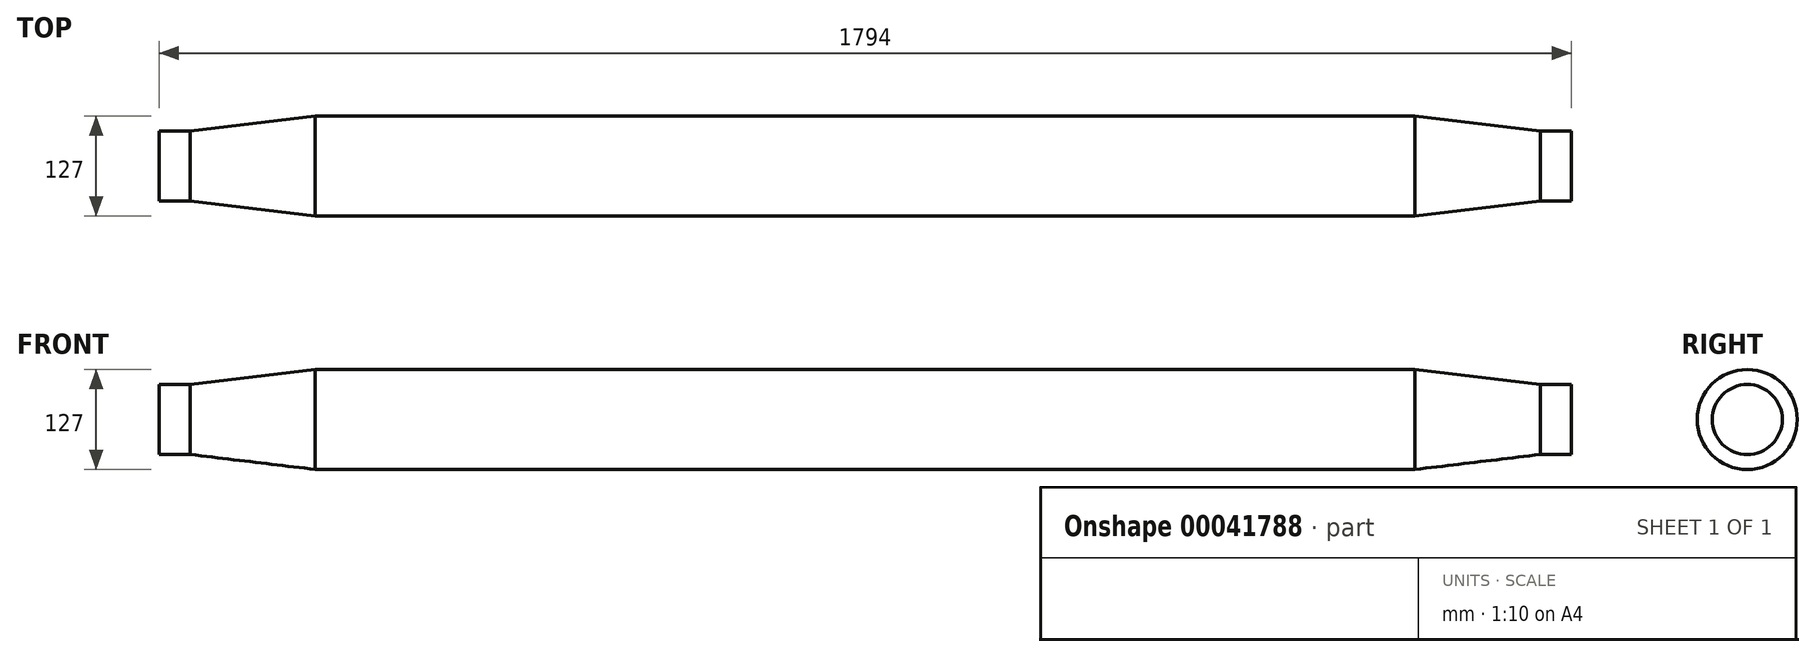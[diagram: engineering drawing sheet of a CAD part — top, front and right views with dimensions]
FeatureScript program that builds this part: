
annotation { "Feature Type Name" : "Feature", "Feature Type Description" : "" }
export const myFeature = defineFeature(function(context is Context, id is Id, definition is map)
    precondition{}
    {
        {
            var Q0;
            Q0=qCreatedBy(makeId("Right.planeOp"),FACE);
            var sketch = newSketch(context, id + "F0", { "sketchPlane" : qUnion([Q0])});
            skCircle(sketch, "E0", {"center": v(0, 0) * mm, "radius": 63.5 * mm});
            skSolve(sketch);
        }
        {
            var Q0;
            Q0=qSketchRegion(id+"F0",true);
            extrude(context, id + "F1", {"entities" : qUnion([Q0]), "endBound" : BoundingType.SYMMETRIC, "depth" : 1397 * mm});
        }
        {
            var Q0;
            Q0=qCreatedBy(makeId("Right.planeOp"),FACE);
            cPlane(context, id + "F2", {"entities" : qUnion([Q0]), "cplaneType" : CPlaneType.OFFSET, "offset" : 897 * mm, "width" : 152.4 * mm, "height" : 152.4 * mm});
        }
        {
            var Q0;
            Q0=qCreatedBy(id+"F2.planeOp",FACE);
            var sketch = newSketch(context, id + "F3", { "sketchPlane" : qUnion([Q0])});
            skCircle(sketch, "E1", {"center": v(0, 0) * mm, "radius": 44.45 * mm});
            skSolve(sketch);
        }
        {
            var Q0;
            Q0=qSketchRegion(id+"F3",true);
            extrude(context, id + "F4", {"entities" : qUnion([Q0]), "oppositeDirection" : true, "depth" : 39.62 * mm});
        }
        {
            var Q0;
            Q0=makeQuery(id+"F4.opExtrude","CAP_FACE",FACE,{"disambiguationData":[OSD([sQuery(id+"F3.wireOp",EDGE,"E1")])],"isStart":false});
            var Q1;
            Q1=makeQuery(id+"F1.opExtrude","CAP_FACE",FACE,{"disambiguationData":[OSD([sQuery(id+"F0.wireOp",EDGE,"E0")])],"isStart":false});
            loft(context, id + "F5", {"sheetProfilesArray" : [{ "sheetProfileEntities" : qUnion([Q0]) }, { "sheetProfileEntities" : qUnion([Q1]) }]});
        }
        {
            var Q0;
            Q0=makeQuery(id+"F5.opLoft","SWEPT_BODY",BODY,{"disambiguationData":[OSD([sQuery(id+"F0.wireOp",EDGE,"E0"),sQuery(id+"F3.wireOp",EDGE,"E1")])]});
            var Q1;
            Q1=makeQuery(id+"F4.opExtrude","SWEPT_BODY",BODY,{"disambiguationData":[OSD([sQuery(id+"F3.wireOp",EDGE,"E1")])]});
            var Q2;
            Q2=qCreatedBy(makeId("Right.planeOp"),FACE);
            mirror(context, id + "F6", {"operationType" : NewBodyOperationType.ADD, "entities" : qUnion([Q0, Q1]), "mirrorPlane" : qUnion([Q2])});
        }
    });
